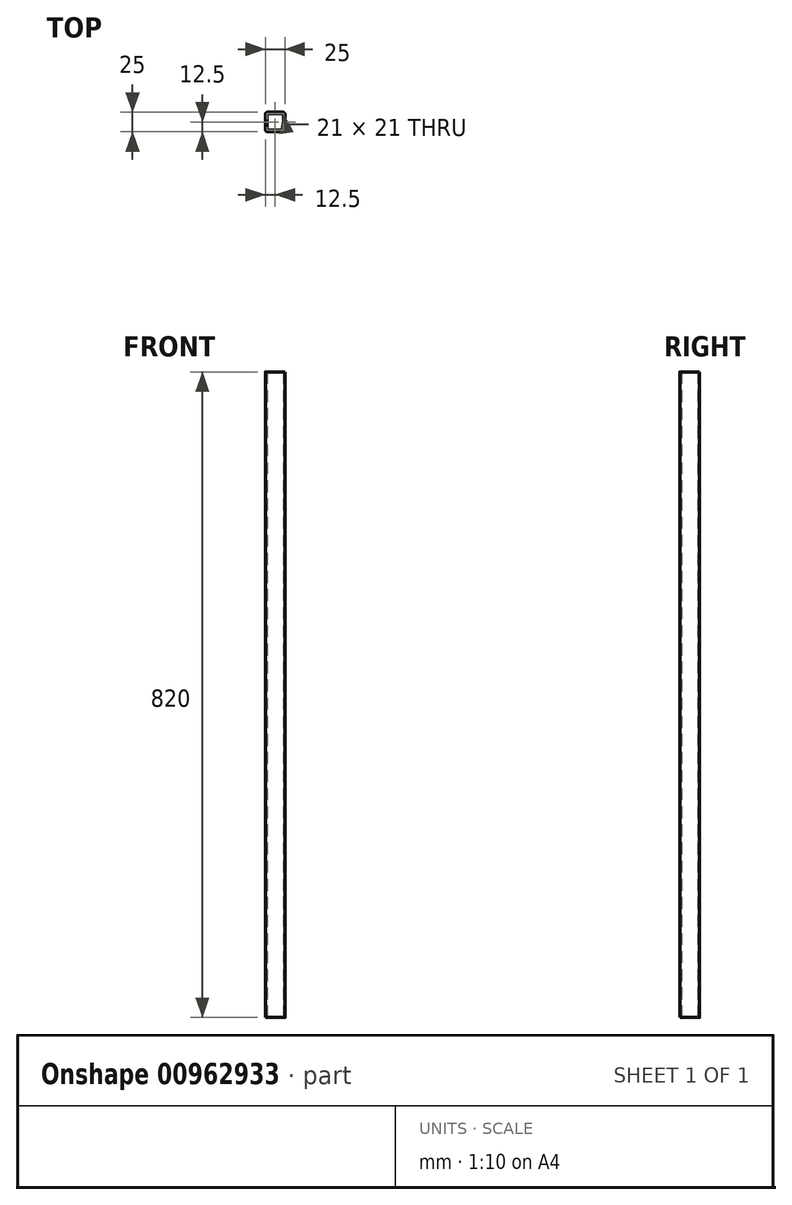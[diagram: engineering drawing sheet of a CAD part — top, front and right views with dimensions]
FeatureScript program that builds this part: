
annotation { "Feature Type Name" : "Feature", "Feature Type Description" : "" }
export const myFeature = defineFeature(function(context is Context, id is Id, definition is map)
    precondition{}
    {
        {
            var Q0;
            Q0=qCreatedBy(makeId("Top.planeOp"),FACE);
            var sketch = newSketch(context, id + "F0", { "sketchPlane" : qUnion([Q0])});
            skLineSegment(sketch, "E0.bottom", {"start": v(9.5, 12.5) * mm, "end": v(-9.5, 12.5) * mm});
            skLineSegment(sketch, "E0.top", {"start": v(9.5, -12.5) * mm, "end": v(-9.5, -12.5) * mm});
            skLineSegment(sketch, "E0.left", {"start": v(12.5, 9.5) * mm, "end": v(12.5, -9.5) * mm});
            skLineSegment(sketch, "E0.right", {"start": v(-12.5, 9.5) * mm, "end": v(-12.5, -9.5) * mm});
            skPoint(sketch, "E0.middle", {"position": v(0, 0) * mm});
            skPoint(sketch, "E1.visualSharp", {"position": v(-12.5, 12.5) * mm});
            skArc(sketch, "E1.filletArc", {"start": v(-9.5, 12.5) * mm, "mid": v(-11.62, 11.62) * mm, "end": v(-12.5, 9.5) * mm});
            skPoint(sketch, "E2.visualSharp", {"position": v(-12.5, -12.5) * mm});
            skArc(sketch, "E2.filletArc", {"start": v(-12.5, -9.5) * mm, "mid": v(-11.62, -11.62) * mm, "end": v(-9.5, -12.5) * mm});
            skPoint(sketch, "E3.visualSharp", {"position": v(12.5, -12.5) * mm});
            skArc(sketch, "E3.filletArc", {"start": v(9.5, -12.5) * mm, "mid": v(11.62, -11.62) * mm, "end": v(12.5, -9.5) * mm});
            skPoint(sketch, "E4.visualSharp", {"position": v(12.5, 12.5) * mm});
            skArc(sketch, "E4.filletArc", {"start": v(12.5, 9.5) * mm, "mid": v(11.62, 11.62) * mm, "end": v(9.5, 12.5) * mm});
            skLineSegment(sketch, "E5.0", {"start": v(10.5, 10.5) * mm, "end": v(-10.5, 10.5) * mm});
            skLineSegment(sketch, "E5.1", {"start": v(10.5, 10.5) * mm, "end": v(10.5, -10.5) * mm});
            skLineSegment(sketch, "E5.2", {"start": v(10.5, -10.5) * mm, "end": v(-10.5, -10.5) * mm});
            skLineSegment(sketch, "E5.3", {"start": v(-10.5, 10.5) * mm, "end": v(-10.5, -10.5) * mm});
            skSolve(sketch);
        }
        {
            var Q0;
            Q0=makeQuery(id+"F0.imprint","IMPRINT",FACE,{"disambiguationData":[TD([[makeQuery(id+"F0.imprint","IMPRINT",EDGE,{"derivedFrom":sQuery(id+"F0.wireOp",EDGE,"E0.bottom")}),1.0]])]});
            extrude(context, id + "F1", {"entities" : qUnion([Q0]), "depth" : 820 * mm, "offsetDistance" : 25 * mm});
        }
    });
